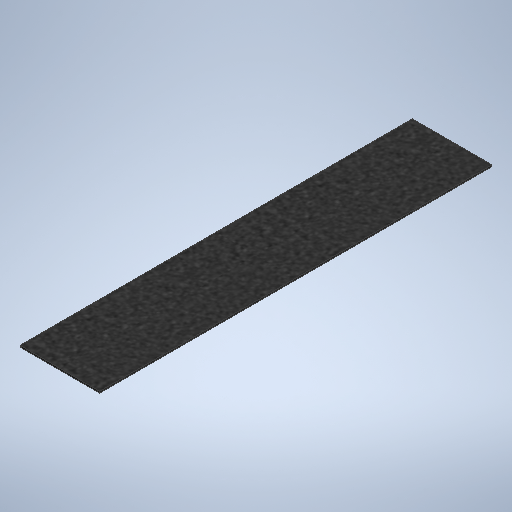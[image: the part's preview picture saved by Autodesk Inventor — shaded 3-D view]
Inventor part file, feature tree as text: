
AUTODESK INVENTOR PART (.ipt)
format: ipt  version: 2025.1 (Build 291241020, 241B)  size: 273,408 bytes
history: native  units: in
note: dims shown in document units (in); Inventor stores cm internally (conversion verified against a paired STEP export)
features: extrude x1, sketch x1
ambient origin geometry x8: Origin, YZ Plane, XZ Plane, XY Plane, X Axis, Y Axis, Z Axis, Center Point
bodies: Solid1 (feature_tree)
feature tree (2):
  extrude  "Extrusion1"  Depth=32.013in
  sketch  "Sketch1"  dims[d0=6.5in d1=32.013in d2=0.125in d3=0.0in]
